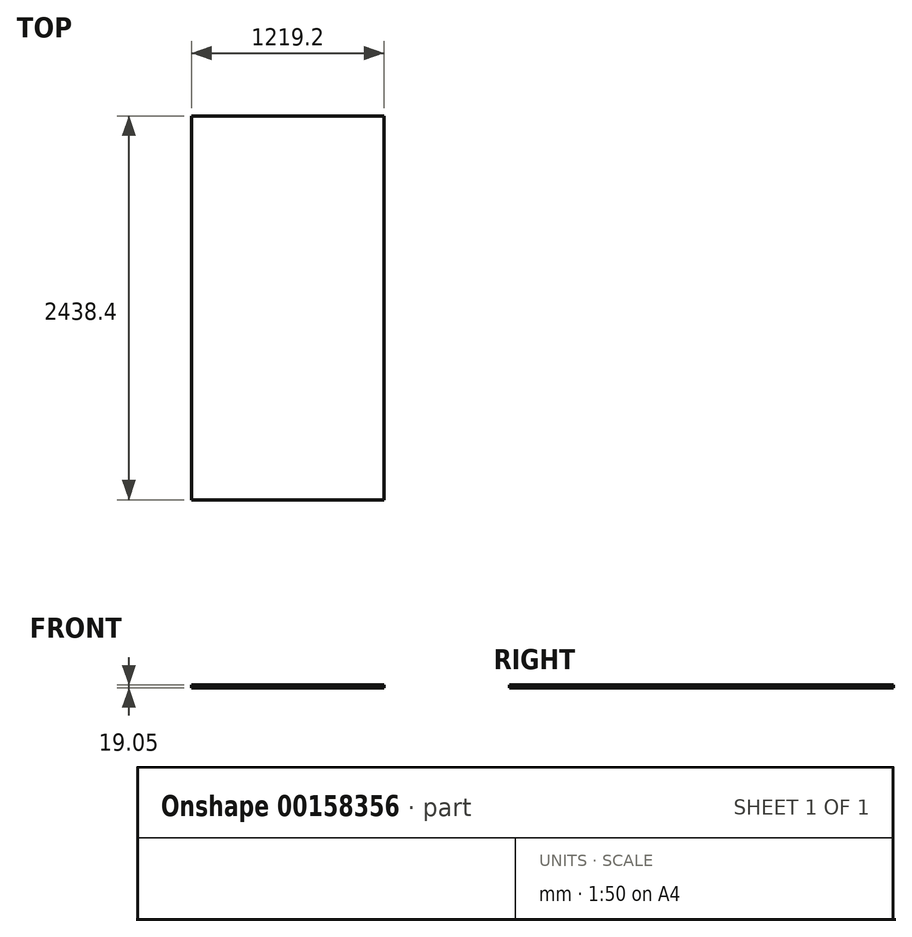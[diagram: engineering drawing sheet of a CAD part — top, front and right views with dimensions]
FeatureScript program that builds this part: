
annotation { "Feature Type Name" : "Feature", "Feature Type Description" : "" }
export const myFeature = defineFeature(function(context is Context, id is Id, definition is map)
    precondition{}
    {
        {
            var Q0;
            Q0=qCreatedBy(makeId("Front.planeOp"),FACE);
            var sketch = newSketch(context, id + "F0", { "sketchPlane" : qUnion([Q0])});
            skLineSegment(sketch, "E0.bottom", {"start": v(-618.13, -63.17) * mm, "end": v(601.07, -63.17) * mm});
            skLineSegment(sketch, "E0.top", {"start": v(-618.13, -82.22) * mm, "end": v(601.07, -82.22) * mm});
            skLineSegment(sketch, "E0.left", {"start": v(-618.13, -63.17) * mm, "end": v(-618.13, -82.22) * mm});
            skLineSegment(sketch, "E0.right", {"start": v(601.07, -63.17) * mm, "end": v(601.07, -82.22) * mm});
            skSolve(sketch);
        }
        {
            var Q0;
            Q0 = qSketchRegion(id + "F0", true);
            extrude(context, id + "F1", {"entities" : qUnion([Q0]), "endBound" : BoundingType.SYMMETRIC, "depth" : 2438.4 * mm});
        }
    });
